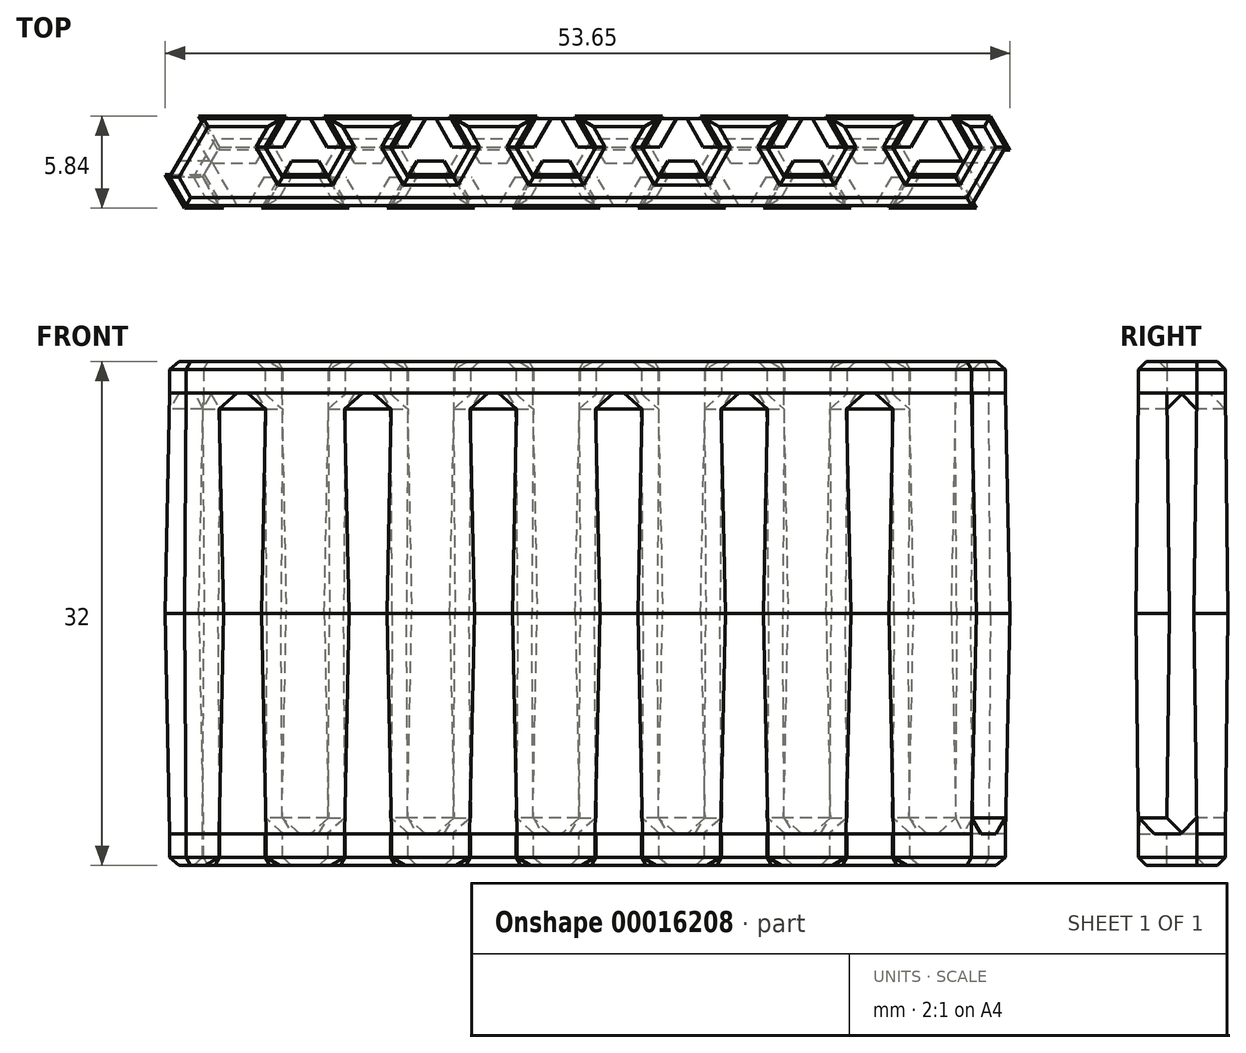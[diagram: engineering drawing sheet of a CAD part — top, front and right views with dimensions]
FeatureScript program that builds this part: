
annotation { "Feature Type Name" : "Feature", "Feature Type Description" : "" }
export const myFeature = defineFeature(function(context is Context, id is Id, definition is map)
    precondition{}
    {
        {
            var Q0;
            Q0=qCreatedBy(makeId("Top.planeOp"),FACE);
            var sketch = newSketch(context, id + "F0", { "sketchPlane" : qUnion([Q0])});
            skLineSegment(sketch, "E0", {"start": v(0, 0) * mm, "end": v(-1.04, 1.8) * mm});
            skLineSegment(sketch, "E1", {"start": v(-1.04, 1.8) * mm, "end": v(0.06, 3.7) * mm});
            skLineSegment(sketch, "E2", {"start": v(0.06, 3.7) * mm, "end": v(2.94, 3.7) * mm});
            skLineSegment(sketch, "E3", {"start": v(2.94, 3.7) * mm, "end": v(4.04, 1.8) * mm});
            skLineSegment(sketch, "E4", {"start": v(4.04, 1.8) * mm, "end": v(3, 0) * mm});
            skLineSegment(sketch, "E5", {"start": v(0.06, 3.7) * mm, "end": v(-0.98, 5.5) * mm});
            skLineSegment(sketch, "E6", {"start": v(2.94, 3.7) * mm, "end": v(3.98, 5.5) * mm});
            skLineSegment(sketch, "E7", {"start": v(1.5, 3.7) * mm, "end": v(1.5, 1.6) * mm, "construction": true});
            skLineSegment(sketch, "E8", {"start": v(1.5, 1.6) * mm, "end": v(3.32, 0.55) * mm, "construction": true});
            skLineSegment(sketch, "E9", {"start": v(1.5, 1.6) * mm, "end": v(-0.32, 0.55) * mm, "construction": true});
            skLineSegment(sketch, "E10", {"start": v(4.04, 1.8) * mm, "end": v(6.93, 1.8) * mm});
            skLineSegment(sketch, "E11", {"start": v(1.5, 1.6) * mm, "end": v(1.5, -0.5) * mm, "construction": true});
            skLineSegment(sketch, "E12", {"start": v(-0.98, 5.5) * mm, "end": v(3.98, 5.5) * mm});
            skLineSegment(sketch, "E13", {"start": v(3, 0) * mm, "end": v(0, 0) * mm});
            skLineSegment(sketch, "E14", {"start": v(3.98, 5.5) * mm, "end": v(6.99, 5.5) * mm});
            skLineSegment(sketch, "E15", {"start": v(3, 0) * mm, "end": v(7.97, 0) * mm});
            skLineSegment(sketch, "E16", {"start": v(-1.04, 1.8) * mm, "end": v(4.04, 1.8) * mm});
            skLineSegment(sketch, "E17", {"start": v(2.94, 3.7) * mm, "end": v(8.03, 3.7) * mm});
            skLineSegment(sketch, "E18.1.0.0", {"start": v(11.95, 5.5) * mm, "end": v(14.95, 5.5) * mm});
            skLineSegment(sketch, "E18.1.0.1", {"start": v(10.91, 3.7) * mm, "end": v(16, 3.7) * mm});
            skLineSegment(sketch, "E18.1.0.2", {"start": v(12, 1.8) * mm, "end": v(14.9, 1.8) * mm});
            skLineSegment(sketch, "E18.1.0.3", {"start": v(10.97, 0) * mm, "end": v(15.93, 0) * mm});
            skLineSegment(sketch, "E18.1.0.4", {"start": v(10.97, 0) * mm, "end": v(7.97, 0) * mm});
            skLineSegment(sketch, "E18.1.0.5", {"start": v(12, 1.8) * mm, "end": v(10.97, 0) * mm});
            skLineSegment(sketch, "E18.1.0.6", {"start": v(6.93, 1.8) * mm, "end": v(12, 1.8) * mm});
            skLineSegment(sketch, "E18.1.0.7", {"start": v(10.91, 3.7) * mm, "end": v(12, 1.8) * mm});
            skLineSegment(sketch, "E18.1.0.8", {"start": v(8.03, 3.7) * mm, "end": v(10.91, 3.7) * mm});
            skLineSegment(sketch, "E18.1.0.9", {"start": v(10.91, 3.7) * mm, "end": v(11.95, 5.5) * mm});
            skLineSegment(sketch, "E18.1.0.10", {"start": v(6.99, 5.5) * mm, "end": v(11.95, 5.5) * mm});
            skLineSegment(sketch, "E18.1.0.11", {"start": v(8.03, 3.7) * mm, "end": v(6.99, 5.5) * mm});
            skLineSegment(sketch, "E18.1.0.12", {"start": v(6.93, 1.8) * mm, "end": v(8.03, 3.7) * mm});
            skLineSegment(sketch, "E18.1.0.13", {"start": v(7.97, 0) * mm, "end": v(6.93, 1.8) * mm});
            skLineSegment(sketch, "E18.2.0.0", {"start": v(19.92, 5.5) * mm, "end": v(22.92, 5.5) * mm});
            skLineSegment(sketch, "E18.2.0.1", {"start": v(18.88, 3.7) * mm, "end": v(23.96, 3.7) * mm});
            skLineSegment(sketch, "E18.2.0.2", {"start": v(19.98, 1.8) * mm, "end": v(22.86, 1.8) * mm});
            skLineSegment(sketch, "E18.2.0.3", {"start": v(18.94, 0) * mm, "end": v(23.9, 0) * mm});
            skLineSegment(sketch, "E18.2.0.4", {"start": v(18.94, 0) * mm, "end": v(15.93, 0) * mm});
            skLineSegment(sketch, "E18.2.0.5", {"start": v(19.98, 1.8) * mm, "end": v(18.94, 0) * mm});
            skLineSegment(sketch, "E18.2.0.6", {"start": v(14.9, 1.8) * mm, "end": v(19.98, 1.8) * mm});
            skLineSegment(sketch, "E18.2.0.7", {"start": v(18.88, 3.7) * mm, "end": v(19.98, 1.8) * mm});
            skLineSegment(sketch, "E18.2.0.8", {"start": v(16, 3.7) * mm, "end": v(18.88, 3.7) * mm});
            skLineSegment(sketch, "E18.2.0.9", {"start": v(18.88, 3.7) * mm, "end": v(19.92, 5.5) * mm});
            skLineSegment(sketch, "E18.2.0.10", {"start": v(14.95, 5.5) * mm, "end": v(19.92, 5.5) * mm});
            skLineSegment(sketch, "E18.2.0.11", {"start": v(16, 3.7) * mm, "end": v(14.95, 5.5) * mm});
            skLineSegment(sketch, "E18.2.0.12", {"start": v(14.9, 1.8) * mm, "end": v(16, 3.7) * mm});
            skLineSegment(sketch, "E18.2.0.13", {"start": v(15.93, 0) * mm, "end": v(14.9, 1.8) * mm});
            skLineSegment(sketch, "E18.3.0.0", {"start": v(27.89, 5.5) * mm, "end": v(30.89, 5.5) * mm});
            skLineSegment(sketch, "E18.3.0.1", {"start": v(26.85, 3.7) * mm, "end": v(31.93, 3.7) * mm});
            skLineSegment(sketch, "E18.3.0.2", {"start": v(27.94, 1.8) * mm, "end": v(30.83, 1.8) * mm});
            skLineSegment(sketch, "E18.3.0.3", {"start": v(26.9, 0) * mm, "end": v(31.87, 0) * mm});
            skLineSegment(sketch, "E18.3.0.4", {"start": v(26.9, 0) * mm, "end": v(23.9, 0) * mm});
            skLineSegment(sketch, "E18.3.0.5", {"start": v(27.94, 1.8) * mm, "end": v(26.9, 0) * mm});
            skLineSegment(sketch, "E18.3.0.6", {"start": v(22.86, 1.8) * mm, "end": v(27.94, 1.8) * mm});
            skLineSegment(sketch, "E18.3.0.7", {"start": v(26.85, 3.7) * mm, "end": v(27.94, 1.8) * mm});
            skLineSegment(sketch, "E18.3.0.8", {"start": v(23.96, 3.7) * mm, "end": v(26.85, 3.7) * mm});
            skLineSegment(sketch, "E18.3.0.9", {"start": v(26.85, 3.7) * mm, "end": v(27.89, 5.5) * mm});
            skLineSegment(sketch, "E18.3.0.10", {"start": v(22.92, 5.5) * mm, "end": v(27.89, 5.5) * mm});
            skLineSegment(sketch, "E18.3.0.11", {"start": v(23.96, 3.7) * mm, "end": v(22.92, 5.5) * mm});
            skLineSegment(sketch, "E18.3.0.12", {"start": v(22.86, 1.8) * mm, "end": v(23.96, 3.7) * mm});
            skLineSegment(sketch, "E18.3.0.13", {"start": v(23.9, 0) * mm, "end": v(22.86, 1.8) * mm});
            skLineSegment(sketch, "E18.4.0.0", {"start": v(35.85, 5.5) * mm, "end": v(38.86, 5.5) * mm});
            skLineSegment(sketch, "E18.4.0.1", {"start": v(34.81, 3.7) * mm, "end": v(39.9, 3.7) * mm});
            skLineSegment(sketch, "E18.4.0.2", {"start": v(35.91, 1.8) * mm, "end": v(38.8, 1.8) * mm});
            skLineSegment(sketch, "E18.4.0.3", {"start": v(34.87, 0) * mm, "end": v(39.84, 0) * mm});
            skLineSegment(sketch, "E18.4.0.4", {"start": v(34.87, 0) * mm, "end": v(31.87, 0) * mm});
            skLineSegment(sketch, "E18.4.0.5", {"start": v(35.91, 1.8) * mm, "end": v(34.87, 0) * mm});
            skLineSegment(sketch, "E18.4.0.6", {"start": v(30.83, 1.8) * mm, "end": v(35.91, 1.8) * mm});
            skLineSegment(sketch, "E18.4.0.7", {"start": v(34.81, 3.7) * mm, "end": v(35.91, 1.8) * mm});
            skLineSegment(sketch, "E18.4.0.8", {"start": v(31.93, 3.7) * mm, "end": v(34.81, 3.7) * mm});
            skLineSegment(sketch, "E18.4.0.9", {"start": v(34.81, 3.7) * mm, "end": v(35.85, 5.5) * mm});
            skLineSegment(sketch, "E18.4.0.10", {"start": v(30.89, 5.5) * mm, "end": v(35.85, 5.5) * mm});
            skLineSegment(sketch, "E18.4.0.11", {"start": v(31.93, 3.7) * mm, "end": v(30.89, 5.5) * mm});
            skLineSegment(sketch, "E18.4.0.12", {"start": v(30.83, 1.8) * mm, "end": v(31.93, 3.7) * mm});
            skLineSegment(sketch, "E18.4.0.13", {"start": v(31.87, 0) * mm, "end": v(30.83, 1.8) * mm});
            skLineSegment(sketch, "E18.5.0.0", {"start": v(43.82, 5.5) * mm, "end": v(46.82, 5.5) * mm});
            skLineSegment(sketch, "E18.5.0.1", {"start": v(42.78, 3.7) * mm, "end": v(47.86, 3.7) * mm});
            skLineSegment(sketch, "E18.5.0.2", {"start": v(43.88, 1.8) * mm, "end": v(46.77, 1.8) * mm});
            skLineSegment(sketch, "E18.5.0.3", {"start": v(42.84, 0) * mm, "end": v(47.8, 0) * mm});
            skLineSegment(sketch, "E18.5.0.4", {"start": v(42.84, 0) * mm, "end": v(39.84, 0) * mm});
            skLineSegment(sketch, "E18.5.0.5", {"start": v(43.88, 1.8) * mm, "end": v(42.84, 0) * mm});
            skLineSegment(sketch, "E18.5.0.6", {"start": v(38.8, 1.8) * mm, "end": v(43.88, 1.8) * mm});
            skLineSegment(sketch, "E18.5.0.7", {"start": v(42.78, 3.7) * mm, "end": v(43.88, 1.8) * mm});
            skLineSegment(sketch, "E18.5.0.8", {"start": v(39.9, 3.7) * mm, "end": v(42.78, 3.7) * mm});
            skLineSegment(sketch, "E18.5.0.9", {"start": v(42.78, 3.7) * mm, "end": v(43.82, 5.5) * mm});
            skLineSegment(sketch, "E18.5.0.10", {"start": v(38.86, 5.5) * mm, "end": v(43.82, 5.5) * mm});
            skLineSegment(sketch, "E18.5.0.11", {"start": v(39.9, 3.7) * mm, "end": v(38.86, 5.5) * mm});
            skLineSegment(sketch, "E18.5.0.12", {"start": v(38.8, 1.8) * mm, "end": v(39.9, 3.7) * mm});
            skLineSegment(sketch, "E18.5.0.13", {"start": v(39.84, 0) * mm, "end": v(38.8, 1.8) * mm});
            skLineSegment(sketch, "E18.direction1", {"start": v(3.98, 5.5) * mm, "end": v(11.95, 5.5) * mm, "construction": true});
            skLineSegment(sketch, "E19", {"start": v(-0.98, 5.5) * mm, "end": v(-3.12, 1.8) * mm});
            skLineSegment(sketch, "E20", {"start": v(-3.12, 1.8) * mm, "end": v(-1.04, 1.8) * mm});
            skLineSegment(sketch, "E21", {"start": v(-3.12, 1.8) * mm, "end": v(-2.08, 0) * mm});
            skLineSegment(sketch, "E22", {"start": v(-2.08, 0) * mm, "end": v(0, 0) * mm});
            skLineSegment(sketch, "E23", {"start": v(46.77, 1.8) * mm, "end": v(47.86, 3.7) * mm});
            skLineSegment(sketch, "E24", {"start": v(46.82, 5.5) * mm, "end": v(47.86, 3.7) * mm});
            skLineSegment(sketch, "E25", {"start": v(46.77, 1.8) * mm, "end": v(47.8, 0) * mm});
            skLineSegment(sketch, "E26", {"start": v(47.8, 0) * mm, "end": v(49.94, 3.7) * mm});
            skLineSegment(sketch, "E27", {"start": v(49.94, 3.7) * mm, "end": v(47.86, 3.7) * mm});
            skLineSegment(sketch, "E28", {"start": v(49.94, 3.7) * mm, "end": v(48.9, 5.5) * mm});
            skLineSegment(sketch, "E29", {"start": v(48.9, 5.5) * mm, "end": v(46.82, 5.5) * mm});
            skLineSegment(sketch, "E30", {"start": v(1.5, 1.6) * mm, "end": v(3.32, 2.65) * mm, "construction": true});
            skSolve(sketch);
        }
        {
            var Q0;
            Q0=makeQuery(id+"F0.imprint","IMPRINT",FACE,{"disambiguationData":[TD([[makeQuery(id+"F0.imprint","IMPRINT",EDGE,{"derivedFrom":sQuery(id+"F0.wireOp",EDGE,"E0")}),1.0]])]});
            var Q1;
            Q1=makeQuery(id+"F0.imprint","IMPRINT",FACE,{"disambiguationData":[TD([[makeQuery(id+"F0.imprint","IMPRINT",EDGE,{"derivedFrom":sQuery(id+"F0.wireOp",EDGE,"E2")}),1.0]])]});
            var Q2;
            Q2=makeQuery(id+"F0.imprint","IMPRINT",FACE,{"disambiguationData":[TD([[makeQuery(id+"F0.imprint","IMPRINT",EDGE,{"derivedFrom":sQuery(id+"F0.wireOp",EDGE,"E6")}),-1.0]])]});
            var Q3;
            Q3=makeQuery(id+"F0.imprint","IMPRINT",FACE,{"disambiguationData":[TD([[makeQuery(id+"F0.imprint","IMPRINT",EDGE,{"derivedFrom":sQuery(id+"F0.wireOp",EDGE,"E3")}),1.0]])]});
            var Q4;
            Q4=makeQuery(id+"F0.imprint","IMPRINT",FACE,{"disambiguationData":[TD([[makeQuery(id+"F0.imprint","IMPRINT",EDGE,{"derivedFrom":sQuery(id+"F0.wireOp",EDGE,"E4")}),1.0]])]});
            var Q5;
            Q5=makeQuery(id+"F0.imprint","IMPRINT",FACE,{"disambiguationData":[TD([[makeQuery(id+"F0.imprint","IMPRINT",EDGE,{"derivedFrom":sQuery(id+"F0.wireOp",EDGE,"E18.1.0.8")}),1.0]])]});
            var Q6;
            Q6=makeQuery(id+"F0.imprint","IMPRINT",FACE,{"disambiguationData":[TD([[makeQuery(id+"F0.imprint","IMPRINT",EDGE,{"derivedFrom":sQuery(id+"F0.wireOp",EDGE,"E18.1.0.0")}),-1.0]])]});
            var Q7;
            Q7=makeQuery(id+"F0.imprint","IMPRINT",FACE,{"disambiguationData":[TD([[makeQuery(id+"F0.imprint","IMPRINT",EDGE,{"derivedFrom":sQuery(id+"F0.wireOp",EDGE,"E18.1.0.1")}),-1.0]])]});
            var Q8;
            Q8=makeQuery(id+"F0.imprint","IMPRINT",FACE,{"disambiguationData":[TD([[makeQuery(id+"F0.imprint","IMPRINT",EDGE,{"derivedFrom":sQuery(id+"F0.wireOp",EDGE,"E18.1.0.2")}),-1.0]])]});
            var Q9;
            Q9=makeQuery(id+"F0.imprint","IMPRINT",FACE,{"disambiguationData":[TD([[makeQuery(id+"F0.imprint","IMPRINT",EDGE,{"derivedFrom":sQuery(id+"F0.wireOp",EDGE,"E18.2.0.8")}),1.0]])]});
            var Q10;
            Q10=makeQuery(id+"F0.imprint","IMPRINT",FACE,{"disambiguationData":[TD([[makeQuery(id+"F0.imprint","IMPRINT",EDGE,{"derivedFrom":sQuery(id+"F0.wireOp",EDGE,"E18.2.0.0")}),-1.0]])]});
            var Q11;
            Q11=makeQuery(id+"F0.imprint","IMPRINT",FACE,{"disambiguationData":[TD([[makeQuery(id+"F0.imprint","IMPRINT",EDGE,{"derivedFrom":sQuery(id+"F0.wireOp",EDGE,"E18.3.0.8")}),1.0]])]});
            var Q12;
            Q12=makeQuery(id+"F0.imprint","IMPRINT",FACE,{"disambiguationData":[TD([[makeQuery(id+"F0.imprint","IMPRINT",EDGE,{"derivedFrom":sQuery(id+"F0.wireOp",EDGE,"E18.3.0.0")}),-1.0]])]});
            var Q13;
            Q13=makeQuery(id+"F0.imprint","IMPRINT",FACE,{"disambiguationData":[TD([[makeQuery(id+"F0.imprint","IMPRINT",EDGE,{"derivedFrom":sQuery(id+"F0.wireOp",EDGE,"E18.4.0.8")}),1.0]])]});
            var Q14;
            Q14=makeQuery(id+"F0.imprint","IMPRINT",FACE,{"disambiguationData":[TD([[makeQuery(id+"F0.imprint","IMPRINT",EDGE,{"derivedFrom":sQuery(id+"F0.wireOp",EDGE,"E18.4.0.0")}),-1.0]])]});
            var Q15;
            Q15=makeQuery(id+"F0.imprint","IMPRINT",FACE,{"disambiguationData":[TD([[makeQuery(id+"F0.imprint","IMPRINT",EDGE,{"derivedFrom":sQuery(id+"F0.wireOp",EDGE,"E18.5.0.8")}),1.0]])]});
            var Q16;
            Q16=makeQuery(id+"F0.imprint","IMPRINT",FACE,{"disambiguationData":[TD([[makeQuery(id+"F0.imprint","IMPRINT",EDGE,{"derivedFrom":sQuery(id+"F0.wireOp",EDGE,"E18.5.0.0")}),-1.0]])]});
            var Q17;
            Q17=makeQuery(id+"F0.imprint","IMPRINT",FACE,{"disambiguationData":[TD([[makeQuery(id+"F0.imprint","IMPRINT",EDGE,{"derivedFrom":sQuery(id+"F0.wireOp",EDGE,"E23")}),-1.0]])]});
            var Q18;
            Q18=makeQuery(id+"F0.imprint","IMPRINT",FACE,{"disambiguationData":[TD([[makeQuery(id+"F0.imprint","IMPRINT",EDGE,{"derivedFrom":sQuery(id+"F0.wireOp",EDGE,"E18.5.0.2")}),-1.0]])]});
            var Q19;
            Q19=makeQuery(id+"F0.imprint","IMPRINT",FACE,{"disambiguationData":[TD([[makeQuery(id+"F0.imprint","IMPRINT",EDGE,{"derivedFrom":sQuery(id+"F0.wireOp",EDGE,"E18.5.0.1")}),-1.0]])]});
            var Q20;
            Q20=makeQuery(id+"F0.imprint","IMPRINT",FACE,{"disambiguationData":[TD([[makeQuery(id+"F0.imprint","IMPRINT",EDGE,{"derivedFrom":sQuery(id+"F0.wireOp",EDGE,"E18.4.0.1")}),-1.0]])]});
            var Q21;
            Q21=makeQuery(id+"F0.imprint","IMPRINT",FACE,{"disambiguationData":[TD([[makeQuery(id+"F0.imprint","IMPRINT",EDGE,{"derivedFrom":sQuery(id+"F0.wireOp",EDGE,"E18.4.0.2")}),-1.0]])]});
            var Q22;
            Q22=makeQuery(id+"F0.imprint","IMPRINT",FACE,{"disambiguationData":[TD([[makeQuery(id+"F0.imprint","IMPRINT",EDGE,{"derivedFrom":sQuery(id+"F0.wireOp",EDGE,"E18.3.0.2")}),-1.0]])]});
            var Q23;
            Q23=makeQuery(id+"F0.imprint","IMPRINT",FACE,{"disambiguationData":[TD([[makeQuery(id+"F0.imprint","IMPRINT",EDGE,{"derivedFrom":sQuery(id+"F0.wireOp",EDGE,"E18.3.0.1")}),-1.0]])]});
            var Q24;
            Q24=makeQuery(id+"F0.imprint","IMPRINT",FACE,{"disambiguationData":[TD([[makeQuery(id+"F0.imprint","IMPRINT",EDGE,{"derivedFrom":sQuery(id+"F0.wireOp",EDGE,"E18.2.0.2")}),-1.0]])]});
            var Q25;
            Q25=makeQuery(id+"F0.imprint","IMPRINT",FACE,{"disambiguationData":[TD([[makeQuery(id+"F0.imprint","IMPRINT",EDGE,{"derivedFrom":sQuery(id+"F0.wireOp",EDGE,"E18.2.0.1")}),-1.0]])]});
            var Q26;
            Q26=makeQuery(id+"F0.imprint","IMPRINT",FACE,{"disambiguationData":[TD([[makeQuery(id+"F0.imprint","IMPRINT",EDGE,{"derivedFrom":sQuery(id+"F0.wireOp",EDGE,"E1")}),1.0]])]});
            var Q27;
            Q27=makeQuery(id+"F0.imprint","IMPRINT",FACE,{"disambiguationData":[TD([[makeQuery(id+"F0.imprint","IMPRINT",EDGE,{"derivedFrom":sQuery(id+"F0.wireOp",EDGE,"E24")}),1.0]])]});
            extrude(context, id + "F1", {"entities" : qUnion([Q0, Q1, Q2, Q3, Q4, Q5, Q6, Q7, Q8, Q9, Q10, Q11, Q12, Q13, Q14, Q15, Q16, Q17, Q18, Q19, Q20, Q21, Q22, Q23, Q24, Q25, Q26, Q27]), "oppositeDirection" : true, "depth" : 2 * mm});
        }
        {
            var Q0;
            Q0=makeQuery(id+"F0.imprint","IMPRINT",FACE,{"disambiguationData":[TD([[makeQuery(id+"F0.imprint","IMPRINT",EDGE,{"derivedFrom":sQuery(id+"F0.wireOp",EDGE,"E0")}),1.0]])]});
            var Q1;
            Q1=makeQuery(id+"F0.imprint","IMPRINT",FACE,{"disambiguationData":[TD([[makeQuery(id+"F0.imprint","IMPRINT",EDGE,{"derivedFrom":sQuery(id+"F0.wireOp",EDGE,"E2")}),1.0]])]});
            var Q2;
            Q2=makeQuery(id+"F0.imprint","IMPRINT",FACE,{"disambiguationData":[TD([[makeQuery(id+"F0.imprint","IMPRINT",EDGE,{"derivedFrom":sQuery(id+"F0.wireOp",EDGE,"E4")}),1.0]])]});
            var Q3;
            Q3=makeQuery(id+"F0.imprint","IMPRINT",FACE,{"disambiguationData":[TD([[makeQuery(id+"F0.imprint","IMPRINT",EDGE,{"derivedFrom":sQuery(id+"F0.wireOp",EDGE,"E18.1.0.8")}),1.0]])]});
            var Q4;
            Q4=makeQuery(id+"F0.imprint","IMPRINT",FACE,{"disambiguationData":[TD([[makeQuery(id+"F0.imprint","IMPRINT",EDGE,{"derivedFrom":sQuery(id+"F0.wireOp",EDGE,"E18.1.0.2")}),-1.0]])]});
            var Q5;
            Q5=makeQuery(id+"F0.imprint","IMPRINT",FACE,{"disambiguationData":[TD([[makeQuery(id+"F0.imprint","IMPRINT",EDGE,{"derivedFrom":sQuery(id+"F0.wireOp",EDGE,"E18.2.0.8")}),1.0]])]});
            var Q6;
            Q6=makeQuery(id+"F0.imprint","IMPRINT",FACE,{"disambiguationData":[TD([[makeQuery(id+"F0.imprint","IMPRINT",EDGE,{"derivedFrom":sQuery(id+"F0.wireOp",EDGE,"E18.2.0.2")}),-1.0]])]});
            var Q7;
            Q7=makeQuery(id+"F0.imprint","IMPRINT",FACE,{"disambiguationData":[TD([[makeQuery(id+"F0.imprint","IMPRINT",EDGE,{"derivedFrom":sQuery(id+"F0.wireOp",EDGE,"E18.3.0.8")}),1.0]])]});
            var Q8;
            Q8=makeQuery(id+"F0.imprint","IMPRINT",FACE,{"disambiguationData":[TD([[makeQuery(id+"F0.imprint","IMPRINT",EDGE,{"derivedFrom":sQuery(id+"F0.wireOp",EDGE,"E18.3.0.2")}),-1.0]])]});
            var Q9;
            Q9=makeQuery(id+"F0.imprint","IMPRINT",FACE,{"disambiguationData":[TD([[makeQuery(id+"F0.imprint","IMPRINT",EDGE,{"derivedFrom":sQuery(id+"F0.wireOp",EDGE,"E18.4.0.8")}),1.0]])]});
            var Q10;
            Q10=makeQuery(id+"F0.imprint","IMPRINT",FACE,{"disambiguationData":[TD([[makeQuery(id+"F0.imprint","IMPRINT",EDGE,{"derivedFrom":sQuery(id+"F0.wireOp",EDGE,"E18.4.0.2")}),-1.0]])]});
            var Q11;
            Q11=makeQuery(id+"F0.imprint","IMPRINT",FACE,{"disambiguationData":[TD([[makeQuery(id+"F0.imprint","IMPRINT",EDGE,{"derivedFrom":sQuery(id+"F0.wireOp",EDGE,"E18.5.0.8")}),1.0]])]});
            var Q12;
            Q12=makeQuery(id+"F0.imprint","IMPRINT",FACE,{"disambiguationData":[TD([[makeQuery(id+"F0.imprint","IMPRINT",EDGE,{"derivedFrom":sQuery(id+"F0.wireOp",EDGE,"E18.5.0.2")}),-1.0]])]});
            var Q13;
            Q13=makeQuery(id+"F0.imprint","IMPRINT",FACE,{"disambiguationData":[TD([[makeQuery(id+"F0.imprint","IMPRINT",EDGE,{"derivedFrom":sQuery(id+"F0.wireOp",EDGE,"E24")}),1.0]])]});
            extrude(context, id + "F2", {"entities" : qUnion([Q0, Q1, Q2, Q3, Q4, Q5, Q6, Q7, Q8, Q9, Q10, Q11, Q12, Q13]), "operationType" : NewBodyOperationType.ADD, "depth" : 14 * mm, "hasDraft" : true, "draftAngle" : 0.7 * degree});
        }
        {
            var Q0;
            Q0=qCreatedBy(makeId("Top.planeOp"),FACE);
            cPlane(context, id + "F3", {"entities" : qUnion([Q0]), "cplaneType" : CPlaneType.OFFSET, "offset" : 28 * mm, "width" : 150 * mm, "height" : 150 * mm});
        }
        {
            var Q0;
            Q0=qCreatedBy(id+"F3.planeOp",FACE);
            var sketch = newSketch(context, id + "F4", { "sketchPlane" : qUnion([Q0])});
            skLineSegment(sketch, "E31.0", {"start": v(0, 0) * mm, "end": v(-1.04, 1.8) * mm});
            skLineSegment(sketch, "E31.1", {"start": v(-1.04, 1.8) * mm, "end": v(0.06, 3.7) * mm});
            skLineSegment(sketch, "E31.2", {"start": v(0.06, 3.7) * mm, "end": v(2.94, 3.7) * mm});
            skLineSegment(sketch, "E31.3", {"start": v(2.94, 3.7) * mm, "end": v(4.04, 1.8) * mm});
            skLineSegment(sketch, "E31.4", {"start": v(4.04, 1.8) * mm, "end": v(3, 0) * mm});
            skLineSegment(sketch, "E31.5", {"start": v(0.06, 3.7) * mm, "end": v(-0.98, 5.5) * mm});
            skLineSegment(sketch, "E31.6", {"start": v(2.94, 3.7) * mm, "end": v(3.98, 5.5) * mm});
            skLineSegment(sketch, "E31.10", {"start": v(4.04, 1.8) * mm, "end": v(6.93, 1.8) * mm});
            skLineSegment(sketch, "E31.12", {"start": v(-0.98, 5.5) * mm, "end": v(3.98, 5.5) * mm});
            skLineSegment(sketch, "E31.13", {"start": v(3, 0) * mm, "end": v(0, 0) * mm});
            skLineSegment(sketch, "E31.14", {"start": v(3.98, 5.5) * mm, "end": v(6.99, 5.5) * mm});
            skLineSegment(sketch, "E31.15", {"start": v(3, 0) * mm, "end": v(7.97, 0) * mm});
            skLineSegment(sketch, "E31.16", {"start": v(-1.04, 1.8) * mm, "end": v(4.04, 1.8) * mm});
            skLineSegment(sketch, "E31.17", {"start": v(2.94, 3.7) * mm, "end": v(8.03, 3.7) * mm});
            skLineSegment(sketch, "E31.18", {"start": v(11.95, 5.5) * mm, "end": v(14.95, 5.5) * mm});
            skLineSegment(sketch, "E31.19", {"start": v(10.91, 3.7) * mm, "end": v(16, 3.7) * mm});
            skLineSegment(sketch, "E31.20", {"start": v(12, 1.8) * mm, "end": v(14.9, 1.8) * mm});
            skLineSegment(sketch, "E31.21", {"start": v(10.97, 0) * mm, "end": v(15.93, 0) * mm});
            skLineSegment(sketch, "E31.22", {"start": v(10.97, 0) * mm, "end": v(7.97, 0) * mm});
            skLineSegment(sketch, "E31.23", {"start": v(12, 1.8) * mm, "end": v(10.97, 0) * mm});
            skLineSegment(sketch, "E31.24", {"start": v(6.93, 1.8) * mm, "end": v(12, 1.8) * mm});
            skLineSegment(sketch, "E31.25", {"start": v(10.91, 3.7) * mm, "end": v(12, 1.8) * mm});
            skLineSegment(sketch, "E31.26", {"start": v(8.03, 3.7) * mm, "end": v(10.91, 3.7) * mm});
            skLineSegment(sketch, "E31.27", {"start": v(10.91, 3.7) * mm, "end": v(11.95, 5.5) * mm});
            skLineSegment(sketch, "E31.28", {"start": v(6.99, 5.5) * mm, "end": v(11.95, 5.5) * mm});
            skLineSegment(sketch, "E31.29", {"start": v(8.03, 3.7) * mm, "end": v(6.99, 5.5) * mm});
            skLineSegment(sketch, "E31.30", {"start": v(6.93, 1.8) * mm, "end": v(8.03, 3.7) * mm});
            skLineSegment(sketch, "E31.31", {"start": v(7.97, 0) * mm, "end": v(6.93, 1.8) * mm});
            skLineSegment(sketch, "E31.32", {"start": v(19.92, 5.5) * mm, "end": v(22.92, 5.5) * mm});
            skLineSegment(sketch, "E31.33", {"start": v(18.88, 3.7) * mm, "end": v(23.96, 3.7) * mm});
            skLineSegment(sketch, "E31.34", {"start": v(19.98, 1.8) * mm, "end": v(22.86, 1.8) * mm});
            skLineSegment(sketch, "E31.35", {"start": v(18.94, 0) * mm, "end": v(23.9, 0) * mm});
            skLineSegment(sketch, "E31.36", {"start": v(18.94, 0) * mm, "end": v(15.93, 0) * mm});
            skLineSegment(sketch, "E31.37", {"start": v(19.98, 1.8) * mm, "end": v(18.94, 0) * mm});
            skLineSegment(sketch, "E31.38", {"start": v(14.9, 1.8) * mm, "end": v(19.98, 1.8) * mm});
            skLineSegment(sketch, "E31.39", {"start": v(18.88, 3.7) * mm, "end": v(19.98, 1.8) * mm});
            skLineSegment(sketch, "E31.40", {"start": v(16, 3.7) * mm, "end": v(18.88, 3.7) * mm});
            skLineSegment(sketch, "E31.41", {"start": v(18.88, 3.7) * mm, "end": v(19.92, 5.5) * mm});
            skLineSegment(sketch, "E31.42", {"start": v(14.95, 5.5) * mm, "end": v(19.92, 5.5) * mm});
            skLineSegment(sketch, "E31.43", {"start": v(16, 3.7) * mm, "end": v(14.95, 5.5) * mm});
            skLineSegment(sketch, "E31.44", {"start": v(14.9, 1.8) * mm, "end": v(16, 3.7) * mm});
            skLineSegment(sketch, "E31.45", {"start": v(15.93, 0) * mm, "end": v(14.9, 1.8) * mm});
            skLineSegment(sketch, "E31.46", {"start": v(27.89, 5.5) * mm, "end": v(30.89, 5.5) * mm});
            skLineSegment(sketch, "E31.47", {"start": v(26.85, 3.7) * mm, "end": v(31.93, 3.7) * mm});
            skLineSegment(sketch, "E31.48", {"start": v(27.94, 1.8) * mm, "end": v(30.83, 1.8) * mm});
            skLineSegment(sketch, "E31.49", {"start": v(26.9, 0) * mm, "end": v(31.87, 0) * mm});
            skLineSegment(sketch, "E31.50", {"start": v(26.9, 0) * mm, "end": v(23.9, 0) * mm});
            skLineSegment(sketch, "E31.51", {"start": v(27.94, 1.8) * mm, "end": v(26.9, 0) * mm});
            skLineSegment(sketch, "E31.52", {"start": v(22.86, 1.8) * mm, "end": v(27.94, 1.8) * mm});
            skLineSegment(sketch, "E31.53", {"start": v(26.85, 3.7) * mm, "end": v(27.94, 1.8) * mm});
            skLineSegment(sketch, "E31.54", {"start": v(23.96, 3.7) * mm, "end": v(26.85, 3.7) * mm});
            skLineSegment(sketch, "E31.55", {"start": v(26.85, 3.7) * mm, "end": v(27.89, 5.5) * mm});
            skLineSegment(sketch, "E31.56", {"start": v(22.92, 5.5) * mm, "end": v(27.89, 5.5) * mm});
            skLineSegment(sketch, "E31.57", {"start": v(23.96, 3.7) * mm, "end": v(22.92, 5.5) * mm});
            skLineSegment(sketch, "E31.58", {"start": v(22.86, 1.8) * mm, "end": v(23.96, 3.7) * mm});
            skLineSegment(sketch, "E31.59", {"start": v(23.9, 0) * mm, "end": v(22.86, 1.8) * mm});
            skLineSegment(sketch, "E31.60", {"start": v(35.85, 5.5) * mm, "end": v(38.86, 5.5) * mm});
            skLineSegment(sketch, "E31.61", {"start": v(34.81, 3.7) * mm, "end": v(39.9, 3.7) * mm});
            skLineSegment(sketch, "E31.62", {"start": v(35.91, 1.8) * mm, "end": v(38.8, 1.8) * mm});
            skLineSegment(sketch, "E31.63", {"start": v(34.87, 0) * mm, "end": v(39.84, 0) * mm});
            skLineSegment(sketch, "E31.64", {"start": v(34.87, 0) * mm, "end": v(31.87, 0) * mm});
            skLineSegment(sketch, "E31.65", {"start": v(35.91, 1.8) * mm, "end": v(34.87, 0) * mm});
            skLineSegment(sketch, "E31.66", {"start": v(30.83, 1.8) * mm, "end": v(35.91, 1.8) * mm});
            skLineSegment(sketch, "E31.67", {"start": v(34.81, 3.7) * mm, "end": v(35.91, 1.8) * mm});
            skLineSegment(sketch, "E31.68", {"start": v(31.93, 3.7) * mm, "end": v(34.81, 3.7) * mm});
            skLineSegment(sketch, "E31.69", {"start": v(34.81, 3.7) * mm, "end": v(35.85, 5.5) * mm});
            skLineSegment(sketch, "E31.70", {"start": v(30.89, 5.5) * mm, "end": v(35.85, 5.5) * mm});
            skLineSegment(sketch, "E31.71", {"start": v(31.93, 3.7) * mm, "end": v(30.89, 5.5) * mm});
            skLineSegment(sketch, "E31.72", {"start": v(30.83, 1.8) * mm, "end": v(31.93, 3.7) * mm});
            skLineSegment(sketch, "E31.73", {"start": v(31.87, 0) * mm, "end": v(30.83, 1.8) * mm});
            skLineSegment(sketch, "E31.74", {"start": v(43.82, 5.5) * mm, "end": v(46.82, 5.5) * mm});
            skLineSegment(sketch, "E31.75", {"start": v(42.78, 3.7) * mm, "end": v(47.86, 3.7) * mm});
            skLineSegment(sketch, "E31.76", {"start": v(43.88, 1.8) * mm, "end": v(46.77, 1.8) * mm});
            skLineSegment(sketch, "E31.77", {"start": v(42.84, 0) * mm, "end": v(47.8, 0) * mm});
            skLineSegment(sketch, "E31.78", {"start": v(42.84, 0) * mm, "end": v(39.84, 0) * mm});
            skLineSegment(sketch, "E31.79", {"start": v(43.88, 1.8) * mm, "end": v(42.84, 0) * mm});
            skLineSegment(sketch, "E31.80", {"start": v(38.8, 1.8) * mm, "end": v(43.88, 1.8) * mm});
            skLineSegment(sketch, "E31.81", {"start": v(42.78, 3.7) * mm, "end": v(43.88, 1.8) * mm});
            skLineSegment(sketch, "E31.82", {"start": v(39.9, 3.7) * mm, "end": v(42.78, 3.7) * mm});
            skLineSegment(sketch, "E31.83", {"start": v(42.78, 3.7) * mm, "end": v(43.82, 5.5) * mm});
            skLineSegment(sketch, "E31.84", {"start": v(38.86, 5.5) * mm, "end": v(43.82, 5.5) * mm});
            skLineSegment(sketch, "E31.85", {"start": v(39.9, 3.7) * mm, "end": v(38.86, 5.5) * mm});
            skLineSegment(sketch, "E31.86", {"start": v(38.8, 1.8) * mm, "end": v(39.9, 3.7) * mm});
            skLineSegment(sketch, "E31.87", {"start": v(39.84, 0) * mm, "end": v(38.8, 1.8) * mm});
            skLineSegment(sketch, "E31.88", {"start": v(3.98, 5.5) * mm, "end": v(11.95, 5.5) * mm});
            skLineSegment(sketch, "E31.89", {"start": v(-0.98, 5.5) * mm, "end": v(-3.12, 1.8) * mm});
            skLineSegment(sketch, "E31.90", {"start": v(-3.12, 1.8) * mm, "end": v(-1.04, 1.8) * mm});
            skLineSegment(sketch, "E31.91", {"start": v(-3.12, 1.8) * mm, "end": v(-2.08, 0) * mm});
            skLineSegment(sketch, "E31.92", {"start": v(-2.08, 0) * mm, "end": v(0, 0) * mm});
            skLineSegment(sketch, "E31.93", {"start": v(46.77, 1.8) * mm, "end": v(47.86, 3.7) * mm});
            skLineSegment(sketch, "E31.94", {"start": v(46.82, 5.5) * mm, "end": v(47.86, 3.7) * mm});
            skLineSegment(sketch, "E31.95", {"start": v(46.77, 1.8) * mm, "end": v(47.8, 0) * mm});
            skLineSegment(sketch, "E31.96", {"start": v(47.8, 0) * mm, "end": v(49.94, 3.7) * mm});
            skLineSegment(sketch, "E31.97", {"start": v(49.94, 3.7) * mm, "end": v(47.86, 3.7) * mm});
            skLineSegment(sketch, "E31.98", {"start": v(49.94, 3.7) * mm, "end": v(48.9, 5.5) * mm});
            skLineSegment(sketch, "E31.99", {"start": v(48.9, 5.5) * mm, "end": v(46.82, 5.5) * mm});
            skSolve(sketch);
        }
        {
            var Q0;
            Q0=makeQuery(id+"F4.imprint","IMPRINT",FACE,{"disambiguationData":[TD([[makeQuery(id+"F4.imprint","IMPRINT",EDGE,{"derivedFrom":sQuery(id+"F4.wireOp",EDGE,"E31.2")}),1.0]])]});
            var Q1;
            Q1=makeQuery(id+"F4.imprint","IMPRINT",FACE,{"disambiguationData":[TD([[makeQuery(id+"F4.imprint","IMPRINT",EDGE,{"derivedFrom":sQuery(id+"F4.wireOp",EDGE,"E31.26")}),1.0]])]});
            var Q2;
            Q2=makeQuery(id+"F4.imprint","IMPRINT",FACE,{"disambiguationData":[TD([[makeQuery(id+"F4.imprint","IMPRINT",EDGE,{"derivedFrom":sQuery(id+"F4.wireOp",EDGE,"E31.40")}),1.0]])]});
            var Q3;
            Q3=makeQuery(id+"F4.imprint","IMPRINT",FACE,{"disambiguationData":[TD([[makeQuery(id+"F4.imprint","IMPRINT",EDGE,{"derivedFrom":sQuery(id+"F4.wireOp",EDGE,"E31.20")}),-1.0]])]});
            var Q4;
            Q4=makeQuery(id+"F4.imprint","IMPRINT",FACE,{"disambiguationData":[TD([[makeQuery(id+"F4.imprint","IMPRINT",EDGE,{"derivedFrom":sQuery(id+"F4.wireOp",EDGE,"E31.4")}),1.0]])]});
            var Q5;
            Q5=makeQuery(id+"F4.imprint","IMPRINT",FACE,{"disambiguationData":[TD([[makeQuery(id+"F4.imprint","IMPRINT",EDGE,{"derivedFrom":sQuery(id+"F4.wireOp",EDGE,"E31.0")}),1.0]])]});
            var Q6;
            Q6=makeQuery(id+"F4.imprint","IMPRINT",FACE,{"disambiguationData":[TD([[makeQuery(id+"F4.imprint","IMPRINT",EDGE,{"derivedFrom":sQuery(id+"F4.wireOp",EDGE,"E31.34")}),-1.0]])]});
            var Q7;
            Q7=makeQuery(id+"F4.imprint","IMPRINT",FACE,{"disambiguationData":[TD([[makeQuery(id+"F4.imprint","IMPRINT",EDGE,{"derivedFrom":sQuery(id+"F4.wireOp",EDGE,"E31.54")}),1.0]])]});
            var Q8;
            Q8=makeQuery(id+"F4.imprint","IMPRINT",FACE,{"disambiguationData":[TD([[makeQuery(id+"F4.imprint","IMPRINT",EDGE,{"derivedFrom":sQuery(id+"F4.wireOp",EDGE,"E31.48")}),-1.0]])]});
            var Q9;
            Q9=makeQuery(id+"F4.imprint","IMPRINT",FACE,{"disambiguationData":[TD([[makeQuery(id+"F4.imprint","IMPRINT",EDGE,{"derivedFrom":sQuery(id+"F4.wireOp",EDGE,"E31.68")}),1.0]])]});
            var Q10;
            Q10=makeQuery(id+"F4.imprint","IMPRINT",FACE,{"disambiguationData":[TD([[makeQuery(id+"F4.imprint","IMPRINT",EDGE,{"derivedFrom":sQuery(id+"F4.wireOp",EDGE,"E31.62")}),-1.0]])]});
            var Q11;
            Q11=makeQuery(id+"F4.imprint","IMPRINT",FACE,{"disambiguationData":[TD([[makeQuery(id+"F4.imprint","IMPRINT",EDGE,{"derivedFrom":sQuery(id+"F4.wireOp",EDGE,"E31.82")}),1.0]])]});
            var Q12;
            Q12=makeQuery(id+"F4.imprint","IMPRINT",FACE,{"disambiguationData":[TD([[makeQuery(id+"F4.imprint","IMPRINT",EDGE,{"derivedFrom":sQuery(id+"F4.wireOp",EDGE,"E31.76")}),-1.0]])]});
            var Q13;
            Q13=makeQuery(id+"F4.imprint","IMPRINT",FACE,{"disambiguationData":[TD([[makeQuery(id+"F4.imprint","IMPRINT",EDGE,{"derivedFrom":sQuery(id+"F4.wireOp",EDGE,"E31.94")}),1.0]])]});
            extrude(context, id + "F5", {"entities" : qUnion([Q0, Q1, Q2, Q3, Q4, Q5, Q6, Q7, Q8, Q9, Q10, Q11, Q12, Q13]), "operationType" : NewBodyOperationType.ADD, "oppositeDirection" : true, "depth" : 14 * mm, "hasDraft" : true, "draftAngle" : 0.7 * degree});
        }
        {
            var Q0;
            Q0=makeQuery(id+"F4.imprint","IMPRINT",FACE,{"disambiguationData":[TD([[makeQuery(id+"F4.imprint","IMPRINT",EDGE,{"derivedFrom":sQuery(id+"F4.wireOp",EDGE,"E31.1")}),-1.0]])]});
            var Q1;
            Q1=makeQuery(id+"F4.imprint","IMPRINT",FACE,{"disambiguationData":[TD([[makeQuery(id+"F4.imprint","IMPRINT",EDGE,{"derivedFrom":sQuery(id+"F4.wireOp",EDGE,"E31.2")}),1.0]])]});
            var Q2;
            Q2=makeQuery(id+"F4.imprint","IMPRINT",FACE,{"disambiguationData":[TD([[makeQuery(id+"F4.imprint","IMPRINT",EDGE,{"derivedFrom":sQuery(id+"F4.wireOp",EDGE,"E31.1")}),1.0]])]});
            var Q3;
            Q3=makeQuery(id+"F4.imprint","IMPRINT",FACE,{"disambiguationData":[TD([[makeQuery(id+"F4.imprint","IMPRINT",EDGE,{"derivedFrom":sQuery(id+"F4.wireOp",EDGE,"E31.0")}),1.0]])]});
            var Q4;
            Q4=makeQuery(id+"F4.imprint","IMPRINT",FACE,{"disambiguationData":[TD([[makeQuery(id+"F4.imprint","IMPRINT",EDGE,{"derivedFrom":sQuery(id+"F4.wireOp",EDGE,"E31.0")}),-1.0]])]});
            var Q5;
            Q5=makeQuery(id+"F4.imprint","IMPRINT",FACE,{"disambiguationData":[TD([[makeQuery(id+"F4.imprint","IMPRINT",EDGE,{"derivedFrom":sQuery(id+"F4.wireOp",EDGE,"E31.4")}),1.0]])]});
            var Q6;
            Q6=makeQuery(id+"F4.imprint","IMPRINT",FACE,{"disambiguationData":[TD([[makeQuery(id+"F4.imprint","IMPRINT",EDGE,{"derivedFrom":sQuery(id+"F4.wireOp",EDGE,"E31.22")}),-1.0]])]});
            var Q7;
            Q7=makeQuery(id+"F4.imprint","IMPRINT",FACE,{"disambiguationData":[TD([[makeQuery(id+"F4.imprint","IMPRINT",EDGE,{"derivedFrom":sQuery(id+"F4.wireOp",EDGE,"E31.24")}),1.0]])]});
            var Q8;
            Q8=makeQuery(id+"F4.imprint","IMPRINT",FACE,{"disambiguationData":[TD([[makeQuery(id+"F4.imprint","IMPRINT",EDGE,{"derivedFrom":sQuery(id+"F4.wireOp",EDGE,"E31.26")}),1.0]])]});
            var Q9;
            Q9=makeQuery(id+"F4.imprint","IMPRINT",FACE,{"disambiguationData":[TD([[makeQuery(id+"F4.imprint","IMPRINT",EDGE,{"derivedFrom":sQuery(id+"F4.wireOp",EDGE,"E31.20")}),-1.0]])]});
            var Q10;
            Q10=makeQuery(id+"F4.imprint","IMPRINT",FACE,{"disambiguationData":[TD([[makeQuery(id+"F4.imprint","IMPRINT",EDGE,{"derivedFrom":sQuery(id+"F4.wireOp",EDGE,"E31.40")}),1.0]])]});
            var Q11;
            Q11=makeQuery(id+"F4.imprint","IMPRINT",FACE,{"disambiguationData":[TD([[makeQuery(id+"F4.imprint","IMPRINT",EDGE,{"derivedFrom":sQuery(id+"F4.wireOp",EDGE,"E31.38")}),1.0]])]});
            var Q12;
            Q12=makeQuery(id+"F4.imprint","IMPRINT",FACE,{"disambiguationData":[TD([[makeQuery(id+"F4.imprint","IMPRINT",EDGE,{"derivedFrom":sQuery(id+"F4.wireOp",EDGE,"E31.36")}),-1.0]])]});
            var Q13;
            Q13=makeQuery(id+"F4.imprint","IMPRINT",FACE,{"disambiguationData":[TD([[makeQuery(id+"F4.imprint","IMPRINT",EDGE,{"derivedFrom":sQuery(id+"F4.wireOp",EDGE,"E31.34")}),-1.0]])]});
            var Q14;
            Q14=makeQuery(id+"F4.imprint","IMPRINT",FACE,{"disambiguationData":[TD([[makeQuery(id+"F4.imprint","IMPRINT",EDGE,{"derivedFrom":sQuery(id+"F4.wireOp",EDGE,"E31.50")}),-1.0]])]});
            var Q15;
            Q15=makeQuery(id+"F4.imprint","IMPRINT",FACE,{"disambiguationData":[TD([[makeQuery(id+"F4.imprint","IMPRINT",EDGE,{"derivedFrom":sQuery(id+"F4.wireOp",EDGE,"E31.52")}),1.0]])]});
            var Q16;
            Q16=makeQuery(id+"F4.imprint","IMPRINT",FACE,{"disambiguationData":[TD([[makeQuery(id+"F4.imprint","IMPRINT",EDGE,{"derivedFrom":sQuery(id+"F4.wireOp",EDGE,"E31.54")}),1.0]])]});
            var Q17;
            Q17=makeQuery(id+"F4.imprint","IMPRINT",FACE,{"disambiguationData":[TD([[makeQuery(id+"F4.imprint","IMPRINT",EDGE,{"derivedFrom":sQuery(id+"F4.wireOp",EDGE,"E31.48")}),-1.0]])]});
            var Q18;
            Q18=makeQuery(id+"F4.imprint","IMPRINT",FACE,{"disambiguationData":[TD([[makeQuery(id+"F4.imprint","IMPRINT",EDGE,{"derivedFrom":sQuery(id+"F4.wireOp",EDGE,"E31.64")}),-1.0]])]});
            var Q19;
            Q19=makeQuery(id+"F4.imprint","IMPRINT",FACE,{"disambiguationData":[TD([[makeQuery(id+"F4.imprint","IMPRINT",EDGE,{"derivedFrom":sQuery(id+"F4.wireOp",EDGE,"E31.66")}),1.0]])]});
            var Q20;
            Q20=makeQuery(id+"F4.imprint","IMPRINT",FACE,{"disambiguationData":[TD([[makeQuery(id+"F4.imprint","IMPRINT",EDGE,{"derivedFrom":sQuery(id+"F4.wireOp",EDGE,"E31.68")}),1.0]])]});
            var Q21;
            Q21=makeQuery(id+"F4.imprint","IMPRINT",FACE,{"disambiguationData":[TD([[makeQuery(id+"F4.imprint","IMPRINT",EDGE,{"derivedFrom":sQuery(id+"F4.wireOp",EDGE,"E31.62")}),-1.0]])]});
            var Q22;
            Q22=makeQuery(id+"F4.imprint","IMPRINT",FACE,{"disambiguationData":[TD([[makeQuery(id+"F4.imprint","IMPRINT",EDGE,{"derivedFrom":sQuery(id+"F4.wireOp",EDGE,"E31.78")}),-1.0]])]});
            var Q23;
            Q23=makeQuery(id+"F4.imprint","IMPRINT",FACE,{"disambiguationData":[TD([[makeQuery(id+"F4.imprint","IMPRINT",EDGE,{"derivedFrom":sQuery(id+"F4.wireOp",EDGE,"E31.80")}),1.0]])]});
            var Q24;
            Q24=makeQuery(id+"F4.imprint","IMPRINT",FACE,{"disambiguationData":[TD([[makeQuery(id+"F4.imprint","IMPRINT",EDGE,{"derivedFrom":sQuery(id+"F4.wireOp",EDGE,"E31.82")}),1.0]])]});
            var Q25;
            Q25=makeQuery(id+"F4.imprint","IMPRINT",FACE,{"disambiguationData":[TD([[makeQuery(id+"F4.imprint","IMPRINT",EDGE,{"derivedFrom":sQuery(id+"F4.wireOp",EDGE,"E31.76")}),-1.0]])]});
            var Q26;
            Q26=makeQuery(id+"F4.imprint","IMPRINT",FACE,{"disambiguationData":[TD([[makeQuery(id+"F4.imprint","IMPRINT",EDGE,{"derivedFrom":sQuery(id+"F4.wireOp",EDGE,"E31.93")}),-1.0]])]});
            var Q27;
            Q27=makeQuery(id+"F4.imprint","IMPRINT",FACE,{"disambiguationData":[TD([[makeQuery(id+"F4.imprint","IMPRINT",EDGE,{"derivedFrom":sQuery(id+"F4.wireOp",EDGE,"E31.94")}),1.0]])]});
            extrude(context, id + "F6", {"entities" : qUnion([Q0, Q1, Q2, Q3, Q4, Q5, Q6, Q7, Q8, Q9, Q10, Q11, Q12, Q13, Q14, Q15, Q16, Q17, Q18, Q19, Q20, Q21, Q22, Q23, Q24, Q25, Q26, Q27]), "operationType" : NewBodyOperationType.ADD, "depth" : 2 * mm});
        }
        {
            var Q0;
            Q0=makeQuery(id+"F2.opExtrude","CAP_EDGE",EDGE,{"disambiguationData":[OSD([sQuery(id+"F0.wireOp",EDGE,"E5")])],"isStart":true});
            var Q1;
            Q1=makeQuery(id+"F2.opExtrude","CAP_EDGE",EDGE,{"disambiguationData":[OSD([sQuery(id+"F0.wireOp",EDGE,"E18.1.0.11")])],"isStart":true});
            var Q2;
            Q2=makeQuery(id+"F2.opExtrude","CAP_EDGE",EDGE,{"disambiguationData":[OSD([sQuery(id+"F0.wireOp",EDGE,"E18.2.0.11")])],"isStart":true});
            var Q3;
            Q3=makeQuery(id+"F2.opExtrude","CAP_EDGE",EDGE,{"disambiguationData":[OSD([sQuery(id+"F0.wireOp",EDGE,"E18.3.0.11")])],"isStart":true});
            var Q4;
            Q4=makeQuery(id+"F2.opExtrude","CAP_EDGE",EDGE,{"disambiguationData":[OSD([sQuery(id+"F0.wireOp",EDGE,"E18.4.0.11")])],"isStart":true});
            var Q5;
            Q5=makeQuery(id+"F2.opExtrude","CAP_EDGE",EDGE,{"disambiguationData":[OSD([sQuery(id+"F0.wireOp",EDGE,"E18.5.0.11")])],"isStart":true});
            var Q6;
            Q6=makeQuery(id+"F2.opExtrude","CAP_EDGE",EDGE,{"disambiguationData":[OSD([sQuery(id+"F0.wireOp",EDGE,"E24")])],"isStart":true});
            var Q7;
            Q7=makeQuery(id+"F2.opExtrude","CAP_EDGE",EDGE,{"disambiguationData":[OSD([sQuery(id+"F0.wireOp",EDGE,"E18.5.0.9")])],"isStart":true});
            var Q8;
            Q8=makeQuery(id+"F2.opExtrude","CAP_EDGE",EDGE,{"disambiguationData":[OSD([sQuery(id+"F0.wireOp",EDGE,"E18.4.0.9")])],"isStart":true});
            var Q9;
            Q9=makeQuery(id+"F2.opExtrude","CAP_EDGE",EDGE,{"disambiguationData":[OSD([sQuery(id+"F0.wireOp",EDGE,"E18.3.0.9")])],"isStart":true});
            var Q10;
            Q10=makeQuery(id+"F2.opExtrude","CAP_EDGE",EDGE,{"disambiguationData":[OSD([sQuery(id+"F0.wireOp",EDGE,"E18.2.0.9")])],"isStart":true});
            var Q11;
            Q11=makeQuery(id+"F2.opExtrude","CAP_EDGE",EDGE,{"disambiguationData":[OSD([sQuery(id+"F0.wireOp",EDGE,"E18.1.0.9")])],"isStart":true});
            var Q12;
            Q12=makeQuery(id+"F2.opExtrude","CAP_EDGE",EDGE,{"disambiguationData":[OSD([sQuery(id+"F0.wireOp",EDGE,"E6")])],"isStart":true});
            var Q13;
            Q13=makeQuery(id+"F2.opExtrude","CAP_EDGE",EDGE,{"disambiguationData":[OSD([sQuery(id+"F0.wireOp",EDGE,"E18.5.0.2")])],"isStart":true});
            var Q14;
            Q14=makeQuery(id+"F2.opExtrude","CAP_EDGE",EDGE,{"disambiguationData":[OSD([sQuery(id+"F0.wireOp",EDGE,"E18.4.0.2")])],"isStart":true});
            var Q15;
            Q15=makeQuery(id+"F2.opExtrude","CAP_EDGE",EDGE,{"disambiguationData":[OSD([sQuery(id+"F0.wireOp",EDGE,"E18.3.0.2")])],"isStart":true});
            var Q16;
            Q16=makeQuery(id+"F2.opExtrude","CAP_EDGE",EDGE,{"disambiguationData":[OSD([sQuery(id+"F0.wireOp",EDGE,"E18.2.0.2")])],"isStart":true});
            var Q17;
            Q17=makeQuery(id+"F2.opExtrude","CAP_EDGE",EDGE,{"disambiguationData":[OSD([sQuery(id+"F0.wireOp",EDGE,"E18.1.0.2")])],"isStart":true});
            var Q18;
            Q18=makeQuery(id+"F2.opExtrude","CAP_EDGE",EDGE,{"disambiguationData":[OSD([sQuery(id+"F0.wireOp",EDGE,"E10")])],"isStart":true});
            var Q19;
            Q19=makeQuery(id+"F2.opExtrude","CAP_EDGE",EDGE,{"disambiguationData":[OSD([sQuery(id+"F0.wireOp",EDGE,"E20")])],"isStart":true});
            var Q20;
            Q20=makeQuery(id+"F5.opExtrude","CAP_EDGE",EDGE,{"disambiguationData":[OSD([sQuery(id+"F4.wireOp",EDGE,"E31.2")])],"isStart":true});
            var Q21;
            Q21=makeQuery(id+"F5.opExtrude","CAP_EDGE",EDGE,{"disambiguationData":[OSD([sQuery(id+"F4.wireOp",EDGE,"E31.26")])],"isStart":true});
            var Q22;
            Q22=makeQuery(id+"F5.opExtrude","CAP_EDGE",EDGE,{"disambiguationData":[OSD([sQuery(id+"F4.wireOp",EDGE,"E31.40")])],"isStart":true});
            var Q23;
            Q23=makeQuery(id+"F5.opExtrude","CAP_EDGE",EDGE,{"disambiguationData":[OSD([sQuery(id+"F4.wireOp",EDGE,"E31.54")])],"isStart":true});
            var Q24;
            Q24=makeQuery(id+"F5.opExtrude","CAP_EDGE",EDGE,{"disambiguationData":[OSD([sQuery(id+"F4.wireOp",EDGE,"E31.68")])],"isStart":true});
            var Q25;
            Q25=makeQuery(id+"F5.opExtrude","CAP_EDGE",EDGE,{"disambiguationData":[OSD([sQuery(id+"F4.wireOp",EDGE,"E31.82")])],"isStart":true});
            var Q26;
            Q26=makeQuery(id+"F5.opExtrude","CAP_EDGE",EDGE,{"disambiguationData":[OSD([sQuery(id+"F4.wireOp",EDGE,"E31.97")])],"isStart":true});
            var Q27;
            Q27=makeQuery(id+"F5.opExtrude","CAP_EDGE",EDGE,{"disambiguationData":[OSD([sQuery(id+"F4.wireOp",EDGE,"E31.0")])],"isStart":true});
            var Q28;
            Q28=makeQuery(id+"F5.opExtrude","CAP_EDGE",EDGE,{"disambiguationData":[OSD([sQuery(id+"F4.wireOp",EDGE,"E31.31")])],"isStart":true});
            var Q29;
            Q29=makeQuery(id+"F5.opExtrude","CAP_EDGE",EDGE,{"disambiguationData":[OSD([sQuery(id+"F4.wireOp",EDGE,"E31.45")])],"isStart":true});
            var Q30;
            Q30=makeQuery(id+"F5.opExtrude","CAP_EDGE",EDGE,{"disambiguationData":[OSD([sQuery(id+"F4.wireOp",EDGE,"E31.59")])],"isStart":true});
            var Q31;
            Q31=makeQuery(id+"F5.opExtrude","CAP_EDGE",EDGE,{"disambiguationData":[OSD([sQuery(id+"F4.wireOp",EDGE,"E31.73")])],"isStart":true});
            var Q32;
            Q32=makeQuery(id+"F5.opExtrude","CAP_EDGE",EDGE,{"disambiguationData":[OSD([sQuery(id+"F4.wireOp",EDGE,"E31.87")])],"isStart":true});
            var Q33;
            Q33=makeQuery(id+"F5.opExtrude","CAP_EDGE",EDGE,{"disambiguationData":[OSD([sQuery(id+"F4.wireOp",EDGE,"E31.95")])],"isStart":true});
            var Q34;
            Q34=makeQuery(id+"F5.opExtrude","CAP_EDGE",EDGE,{"disambiguationData":[OSD([sQuery(id+"F4.wireOp",EDGE,"E31.4")])],"isStart":true});
            var Q35;
            Q35=makeQuery(id+"F5.opExtrude","CAP_EDGE",EDGE,{"disambiguationData":[OSD([sQuery(id+"F4.wireOp",EDGE,"E31.23")])],"isStart":true});
            var Q36;
            Q36=makeQuery(id+"F5.opExtrude","CAP_EDGE",EDGE,{"disambiguationData":[OSD([sQuery(id+"F4.wireOp",EDGE,"E31.37")])],"isStart":true});
            var Q37;
            Q37=makeQuery(id+"F5.opExtrude","CAP_EDGE",EDGE,{"disambiguationData":[OSD([sQuery(id+"F4.wireOp",EDGE,"E31.51")])],"isStart":true});
            var Q38;
            Q38=makeQuery(id+"F5.opExtrude","CAP_EDGE",EDGE,{"disambiguationData":[OSD([sQuery(id+"F4.wireOp",EDGE,"E31.65")])],"isStart":true});
            var Q39;
            Q39=makeQuery(id+"F5.opExtrude","CAP_EDGE",EDGE,{"disambiguationData":[OSD([sQuery(id+"F4.wireOp",EDGE,"E31.79")])],"isStart":true});
            var Q40;
            Q40=makeQuery(id+"F5.opExtrude","CAP_EDGE",EDGE,{"disambiguationData":[OSD([sQuery(id+"F4.wireOp",EDGE,"E31.90")])],"isStart":true});
            var Q41;
            Q41=makeQuery(id+"F2.opExtrude","CAP_EDGE",EDGE,{"disambiguationData":[OSD([sQuery(id+"F0.wireOp",EDGE,"E27")])],"isStart":true});
            var Q42;
            Q42=makeQuery(id+"F2.opExtrude","CAP_EDGE",EDGE,{"disambiguationData":[OSD([sQuery(id+"F0.wireOp",EDGE,"E25")])],"isStart":true});
            var Q43;
            Q43=makeQuery(id+"F5.opExtrude","CAP_EDGE",EDGE,{"disambiguationData":[OSD([sQuery(id+"F4.wireOp",EDGE,"E31.5")])],"isStart":true});
            chamfer(context, id + "F7", {"entities" : qUnion([Q0, Q1, Q2, Q3, Q4, Q5, Q6, Q7, Q8, Q9, Q10, Q11, Q12, Q13, Q14, Q15, Q16, Q17, Q18, Q19, Q20, Q21, Q22, Q23, Q24, Q25, Q26, Q27, Q28, Q29, Q30, Q31, Q32, Q33, Q34, Q35, Q36, Q37, Q38, Q39, Q40, Q41, Q42, Q43]), "width" : 1 * mm, "tangentPropagation" : true});
        }
        {
            var Q0;
            Q0=makeQuery(id+"F1.opExtrude","CAP_FACE",FACE,{"disambiguationData":[OSD([sQuery(id+"F0.wireOp",EDGE,"E0"),sQuery(id+"F0.wireOp",EDGE,"E1"),sQuery(id+"F0.wireOp",EDGE,"E2"),sQuery(id+"F0.wireOp",EDGE,"E3"),sQuery(id+"F0.wireOp",EDGE,"E4"),sQuery(id+"F0.wireOp",EDGE,"E12"),sQuery(id+"F0.wireOp",EDGE,"E14"),sQuery(id+"F0.wireOp",EDGE,"E15"),sQuery(id+"F0.wireOp",EDGE,"E18.1.0.0"),sQuery(id+"F0.wireOp",EDGE,"E18.1.0.3"),sQuery(id+"F0.wireOp",EDGE,"E18.1.0.5"),sQuery(id+"F0.wireOp",EDGE,"E18.1.0.7"),sQuery(id+"F0.wireOp",EDGE,"E18.1.0.8"),sQuery(id+"F0.wireOp",EDGE,"E18.1.0.10"),sQuery(id+"F0.wireOp",EDGE,"E18.1.0.12"),sQuery(id+"F0.wireOp",EDGE,"E18.1.0.13"),sQuery(id+"F0.wireOp",EDGE,"E18.2.0.0"),sQuery(id+"F0.wireOp",EDGE,"E18.2.0.3"),sQuery(id+"F0.wireOp",EDGE,"E18.2.0.5"),sQuery(id+"F0.wireOp",EDGE,"E18.2.0.7"),sQuery(id+"F0.wireOp",EDGE,"E18.2.0.8"),sQuery(id+"F0.wireOp",EDGE,"E18.2.0.10"),sQuery(id+"F0.wireOp",EDGE,"E18.2.0.12"),sQuery(id+"F0.wireOp",EDGE,"E18.2.0.13"),sQuery(id+"F0.wireOp",EDGE,"E18.3.0.0"),sQuery(id+"F0.wireOp",EDGE,"E18.3.0.3"),sQuery(id+"F0.wireOp",EDGE,"E18.3.0.5"),sQuery(id+"F0.wireOp",EDGE,"E18.3.0.7"),sQuery(id+"F0.wireOp",EDGE,"E18.3.0.8"),sQuery(id+"F0.wireOp",EDGE,"E18.3.0.10"),sQuery(id+"F0.wireOp",EDGE,"E18.3.0.12"),sQuery(id+"F0.wireOp",EDGE,"E18.3.0.13"),sQuery(id+"F0.wireOp",EDGE,"E18.4.0.0"),sQuery(id+"F0.wireOp",EDGE,"E18.4.0.3"),sQuery(id+"F0.wireOp",EDGE,"E18.4.0.5"),sQuery(id+"F0.wireOp",EDGE,"E18.4.0.7"),sQuery(id+"F0.wireOp",EDGE,"E18.4.0.8"),sQuery(id+"F0.wireOp",EDGE,"E18.4.0.10"),sQuery(id+"F0.wireOp",EDGE,"E18.4.0.12"),sQuery(id+"F0.wireOp",EDGE,"E18.4.0.13"),sQuery(id+"F0.wireOp",EDGE,"E18.5.0.0"),sQuery(id+"F0.wireOp",EDGE,"E18.5.0.3"),sQuery(id+"F0.wireOp",EDGE,"E18.5.0.5"),sQuery(id+"F0.wireOp",EDGE,"E18.5.0.7"),sQuery(id+"F0.wireOp",EDGE,"E18.5.0.8"),sQuery(id+"F0.wireOp",EDGE,"E18.5.0.10"),sQuery(id+"F0.wireOp",EDGE,"E18.5.0.12"),sQuery(id+"F0.wireOp",EDGE,"E18.5.0.13"),sQuery(id+"F0.wireOp",EDGE,"E19"),sQuery(id+"F0.wireOp",EDGE,"E21"),sQuery(id+"F0.wireOp",EDGE,"E22"),sQuery(id+"F0.wireOp",EDGE,"E26"),sQuery(id+"F0.wireOp",EDGE,"E28"),sQuery(id+"F0.wireOp",EDGE,"E29")])],"isStart":false});
            var Q1;
            Q1=makeQuery(id+"F6.opExtrude","CAP_FACE",FACE,{"disambiguationData":[OSD([sQuery(id+"F4.wireOp",EDGE,"E31.3"),sQuery(id+"F4.wireOp",EDGE,"E31.6"),sQuery(id+"F4.wireOp",EDGE,"E31.10"),sQuery(id+"F4.wireOp",EDGE,"E31.12"),sQuery(id+"F4.wireOp",EDGE,"E31.13"),sQuery(id+"F4.wireOp",EDGE,"E31.15"),sQuery(id+"F4.wireOp",EDGE,"E31.20"),sQuery(id+"F4.wireOp",EDGE,"E31.21"),sQuery(id+"F4.wireOp",EDGE,"E31.22"),sQuery(id+"F4.wireOp",EDGE,"E31.25"),sQuery(id+"F4.wireOp",EDGE,"E31.27"),sQuery(id+"F4.wireOp",EDGE,"E31.29"),sQuery(id+"F4.wireOp",EDGE,"E31.30"),sQuery(id+"F4.wireOp",EDGE,"E31.34"),sQuery(id+"F4.wireOp",EDGE,"E31.35"),sQuery(id+"F4.wireOp",EDGE,"E31.36"),sQuery(id+"F4.wireOp",EDGE,"E31.39"),sQuery(id+"F4.wireOp",EDGE,"E31.41"),sQuery(id+"F4.wireOp",EDGE,"E31.42"),sQuery(id+"F4.wireOp",EDGE,"E31.43"),sQuery(id+"F4.wireOp",EDGE,"E31.44"),sQuery(id+"F4.wireOp",EDGE,"E31.48"),sQuery(id+"F4.wireOp",EDGE,"E31.49"),sQuery(id+"F4.wireOp",EDGE,"E31.50"),sQuery(id+"F4.wireOp",EDGE,"E31.53"),sQuery(id+"F4.wireOp",EDGE,"E31.55"),sQuery(id+"F4.wireOp",EDGE,"E31.56"),sQuery(id+"F4.wireOp",EDGE,"E31.57"),sQuery(id+"F4.wireOp",EDGE,"E31.58"),sQuery(id+"F4.wireOp",EDGE,"E31.62"),sQuery(id+"F4.wireOp",EDGE,"E31.63"),sQuery(id+"F4.wireOp",EDGE,"E31.64"),sQuery(id+"F4.wireOp",EDGE,"E31.67"),sQuery(id+"F4.wireOp",EDGE,"E31.69"),sQuery(id+"F4.wireOp",EDGE,"E31.70"),sQuery(id+"F4.wireOp",EDGE,"E31.71"),sQuery(id+"F4.wireOp",EDGE,"E31.72"),sQuery(id+"F4.wireOp",EDGE,"E31.76"),sQuery(id+"F4.wireOp",EDGE,"E31.77"),sQuery(id+"F4.wireOp",EDGE,"E31.78"),sQuery(id+"F4.wireOp",EDGE,"E31.81"),sQuery(id+"F4.wireOp",EDGE,"E31.83"),sQuery(id+"F4.wireOp",EDGE,"E31.84"),sQuery(id+"F4.wireOp",EDGE,"E31.85"),sQuery(id+"F4.wireOp",EDGE,"E31.86"),sQuery(id+"F4.wireOp",EDGE,"E31.88"),sQuery(id+"F4.wireOp",EDGE,"E31.89"),sQuery(id+"F4.wireOp",EDGE,"E31.91"),sQuery(id+"F4.wireOp",EDGE,"E31.92"),sQuery(id+"F4.wireOp",EDGE,"E31.93"),sQuery(id+"F4.wireOp",EDGE,"E31.94"),sQuery(id+"F4.wireOp",EDGE,"E31.96"),sQuery(id+"F4.wireOp",EDGE,"E31.98"),sQuery(id+"F4.wireOp",EDGE,"E31.99")])],"isStart":false});
            chamfer(context, id + "F8", {"entities" : qUnion([Q0, Q1]), "width" : 0.5 * mm, "tangentPropagation" : true});
        }
    });
